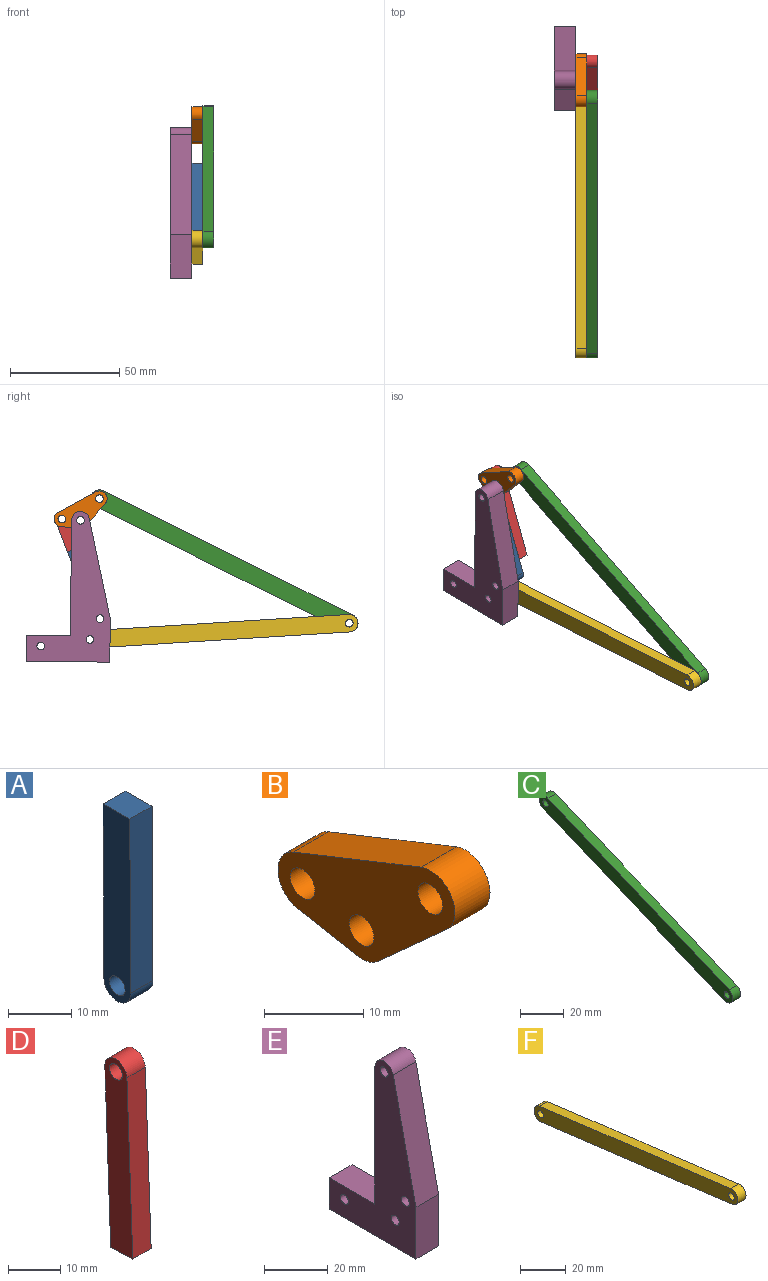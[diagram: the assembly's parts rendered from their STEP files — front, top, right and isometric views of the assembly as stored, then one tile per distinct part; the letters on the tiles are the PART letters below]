
ASSEMBLY  parts=6 mates=7
PART A: 7 faces, bbox 5x6.2x36.8 mm
  f0: cylinder r=3mm len=6mm, axis (1,0,0), area 47.1mm2, adj f1,f3,f5,f6
  f1: plane 33.78x5mm, normal (0,1,-0.01), area 168.9mm2, adj f0,f2,f5,f6
  f2: plane 6x5mm, normal (0,0.01,1), area 30mm2, adj f1,f3,f5,f6
  f3: plane 33.78x5mm, normal (0,-1,0.01), area 168.9mm2, adj f0,f2,f5,f6
  f4: cylinder r=1.75mm len=5mm, axis (1,0,0), area 55mm2, adj f5,f6
  f5: plane 36.8x6.19mm, normal (1,0,0), area 207.2mm2, adj f0,f1,f2,f3,f4
  f6: plane 36.8x6.19mm, normal (-1,0,0), area 207.2mm2, adj f0,f1,f2,f3,f4
PART B: 11 faces, bbox 5x25.2x15.8 mm
  f0: plane 18.16x7.22mm, normal (0,0.37,0.93), area 97.7mm2, adj f1,f8,f9,f10
  f1: cylinder r=3.5mm len=6.1mm, axis (1,0,0), area 48.8mm2, adj f0,f2,f9,f10
  f2: plane 9.76x8.79mm, normal (0,-0.67,-0.74), area 65.7mm2, adj f1,f3,f9,f10
  f3: cylinder r=3.5mm len=5mm, axis (1,0,0), area 16.1mm2, adj f2,f4,f9,f10
  f4: plane 8.4x5mm, normal (0,0.18,-0.98), area 42.7mm2, adj f3,f8,f9,f10
  f5: cylinder r=1.75mm len=5mm, axis (1,0,0), area 55mm2, adj f9,f10
  f6: cylinder r=1.75mm len=5mm, axis (1,0,0), area 55mm2, adj f9,f10
  f7: cylinder r=1.75mm len=5mm, axis (1,0,0), area 55mm2, adj f9,f10
  f8: cylinder r=3.5mm len=6.69mm, axis (1,0,0), area 45.1mm2, adj f0,f4,f9,f10
  f9: plane 25.16x15.79mm, normal (1,0,0), area 198.6mm2, adj f0,f1,f2,f3,f4,f5,f6,f7
  f10: plane 25.16x15.79mm, normal (-1,0,0), area 198.6mm2, adj f0,f1,f2,f3,f4,f5,f6,f7
PART C: 8 faces, bbox 5x125.7x57 mm
  f0: plane 117.7x48.98mm, normal (0,0.38,-0.92), area 637.4mm2, adj f1,f5,f6,f7
  f1: cylinder r=4mm len=7.69mm, axis (1,0,0), area 62.8mm2, adj f0,f2,f6,f7
  f2: plane 117.7x48.98mm, normal (0,-0.38,0.92), area 637.4mm2, adj f1,f5,f6,f7
  f3: cylinder r=1.75mm len=5mm, axis (1,0,0), area 55mm2, adj f6,f7
  f4: cylinder r=1.75mm len=5mm, axis (1,0,0), area 55mm2, adj f6,f7
  f5: cylinder r=4mm len=7.69mm, axis (1,0,0), area 62.8mm2, adj f0,f2,f6,f7
  f6: plane 125.7x56.98mm, normal (1,0,0), area 1050.9mm2, adj f0,f1,f2,f3,f4,f5
  f7: plane 125.7x56.98mm, normal (-1,0,0), area 1050.9mm2, adj f0,f1,f2,f3,f4,f5
PART D: 7 faces, bbox 5x7.6x45 mm
  f0: plane 6x5mm, normal (0,-0.04,-1), area 30mm2, adj f1,f4,f5,f6
  f1: plane 41.88x5mm, normal (0,1,-0.04), area 209.5mm2, adj f0,f2,f5,f6
  f2: cylinder r=3mm len=6mm, axis (1,0,0), area 47.1mm2, adj f1,f4,f5,f6
  f3: cylinder r=1.75mm len=5mm, axis (1,0,0), area 55mm2, adj f5,f6
  f4: plane 41.88x5mm, normal (0,-1,0.04), area 209.5mm2, adj f0,f2,f5,f6
  f5: plane 44.99x7.59mm, normal (1,0,0), area 256mm2, adj f0,f1,f2,f3,f4
  f6: plane 44.99x7.59mm, normal (-1,0,0), area 256mm2, adj f0,f1,f2,f3,f4
PART E: 13 faces, bbox 10x38.3x68.7 mm
  f0: plane 11.98x10mm, normal (0,1,0), area 119.8mm2, adj f1,f10,f11,f12
  f1: plane 38.27x10mm, normal (0,0,-1), area 382.7mm2, adj f0,f2,f11,f12
  f2: plane 19.81x10mm, normal (0,-1,0), area 198.1mm2, adj f1,f3,f11,f12
  f3: plane 45.69x10.06mm, normal (0,-0.98,0.22), area 467.8mm2, adj f2,f4,f11,f12
  f4: cylinder r=4.08mm len=10mm, axis (-1,0,0), area 119.4mm2, adj f3,f5,f11,f12
  f5: plane 52.64x10mm, normal (0,1,0), area 526.4mm2, adj f4,f10,f11,f12
  f6: cylinder r=1.75mm len=10mm, axis (-1,0,0), area 110mm2, adj f11,f12
  f7: cylinder r=1.75mm len=10mm, axis (-1,0,0), area 110mm2, adj f11,f12
  f8: cylinder r=1.75mm len=10mm, axis (-1,0,0), area 110mm2, adj f11,f12
  f9: cylinder r=1.75mm len=10mm, axis (-1,0,0), area 110mm2, adj f11,f12
  f10: plane 20.15x10mm, normal (0,0,1), area 201.5mm2, adj f0,f5,f11,f12
  f11: plane 68.7x38.27mm, normal (-1,0,0), area 1179.4mm2, adj f0,f1,f2,f3,f4,f5,f6,f7
  f12: plane 68.7x38.27mm, normal (1,0,0), area 1179.4mm2, adj f0,f1,f2,f3,f4,f5,f6,f7
PART F: 8 faces, bbox 5x125.7x22.9 mm
  f0: plane 117.72x14.88mm, normal (0,-0.13,-0.99), area 593.3mm2, adj f1,f5,f6,f7
  f1: cylinder r=4mm len=7.97mm, axis (1,0,0), area 62.8mm2, adj f0,f2,f6,f7
  f2: plane 117.72x14.88mm, normal (0,0.13,0.99), area 593.3mm2, adj f1,f5,f6,f7
  f3: cylinder r=1.75mm len=5mm, axis (1,0,0), area 55mm2, adj f6,f7
  f4: cylinder r=1.75mm len=5mm, axis (1,0,0), area 55mm2, adj f6,f7
  f5: cylinder r=4mm len=7.97mm, axis (1,0,0), area 62.8mm2, adj f0,f2,f6,f7
  f6: plane 125.72x22.88mm, normal (1,0,0), area 980.3mm2, adj f0,f1,f2,f3,f4,f5
  f7: plane 125.72x22.88mm, normal (-1,0,0), area 980.3mm2, adj f0,f1,f2,f3,f4,f5
PLACE A rot(axis=(-1,0,0),20.7deg) t=(2.62,-30.95,6.75)mm
PLACE B rot(axis=(-1,0,0),6.9deg) t=(2.62,-19.65,-13.9)mm
PLACE C rot(axis=(1,0,0),3.9deg) t=(2.62,-9.53,-15.37)mm
PLACE D rot(axis=(-1,0,0),18.8deg) t=(2.62,-27.96,-6.77)mm
PLACE E rot(axis=(1,0,0),0.6deg) t=(2.62,-10.5,-16.02)mm fixed
PLACE F rot(axis=(1,0,0),3.6deg) t=(2.62,-9.52,-15.94)mm
MATE revolute D.f2 <-> B.f5  axis (-1,0,0) through (2.62,10.36,29.47)mm
MATE planar A.f1 <-> D.f1  axis (0,0.93,-0.36) through (0.12,1.77,-1.29)mm
MATE revolute C.f1 <-> B.f1  axis (-1,0,0) through (2.62,-6.8,38.83)mm
MATE revolute B.f3 <-> E.f4  axis (-1,0,0) through (-2.38,1.83,28.92)mm
MATE revolute E.f7 <-> F.f1  axis (1,0,0) through (-2.38,-2.46,-25.49)mm
MATE revolute F.f3 <-> C.f3  axis (1,0,0) through (2.62,-120.89,-18.07)mm
MATE revolute A.f0 <-> E.f6  axis (1,0,0) through (-2.38,-7.08,-15.98)mm
